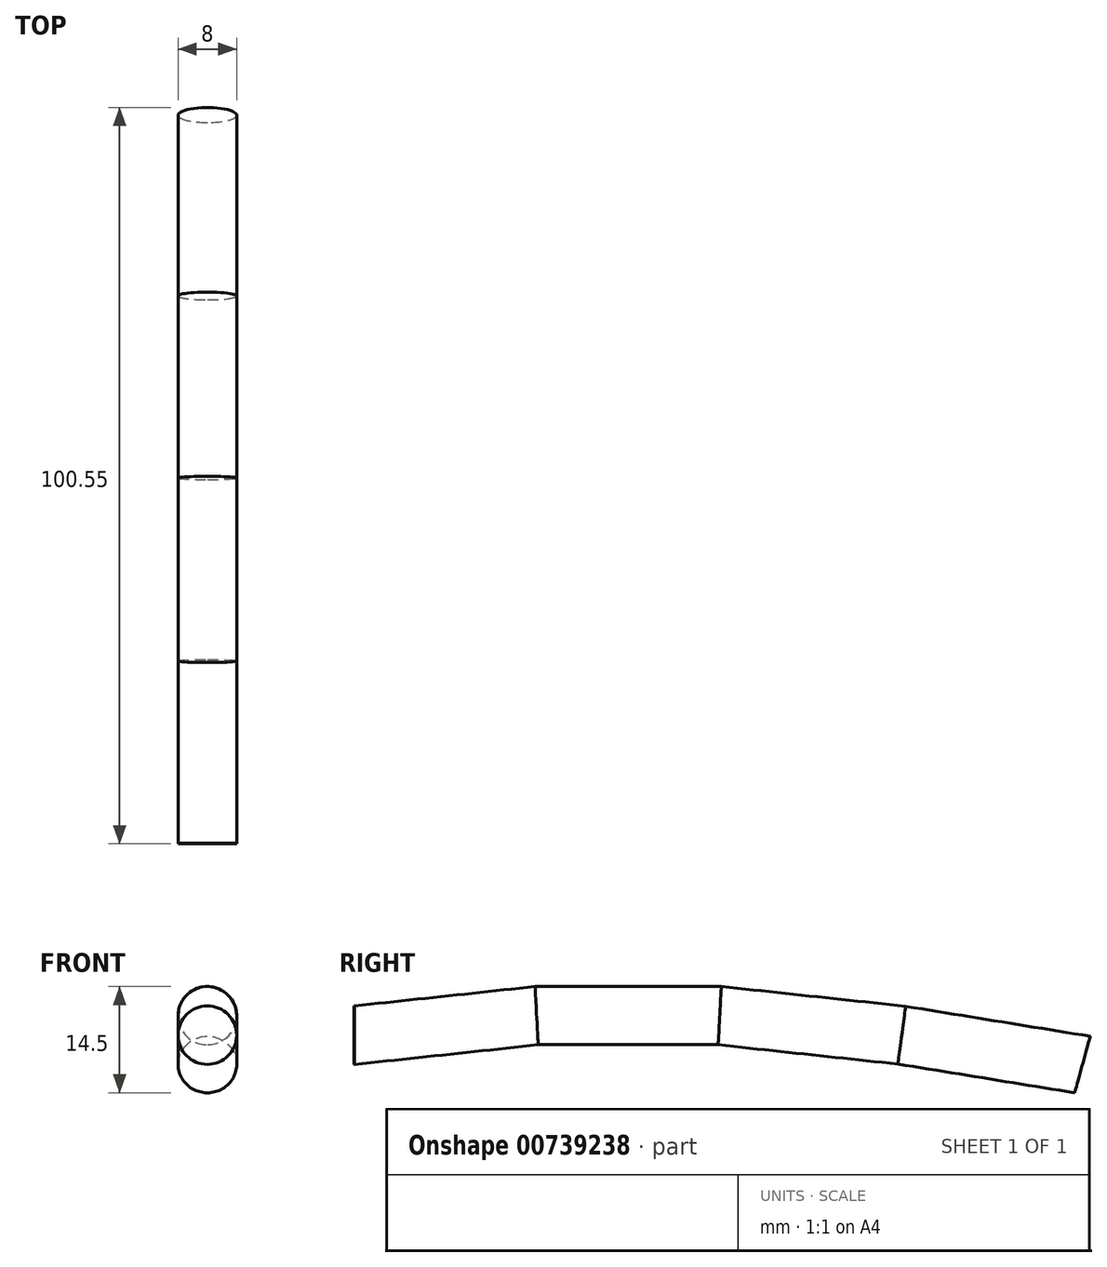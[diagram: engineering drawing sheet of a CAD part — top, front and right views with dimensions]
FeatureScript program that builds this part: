
annotation { "Feature Type Name" : "Feature", "Feature Type Description" : "" }
export const myFeature = defineFeature(function(context is Context, id is Id, definition is map)
    precondition{}
    {
        {
            var Q0;
            Q0=qCreatedBy(makeId("Front.planeOp"),FACE);
            var sketch = newSketch(context, id + "F0", { "sketchPlane" : qUnion([Q0])});
            skCircle(sketch, "E0", {"center": v(-0.51, 0) * mm, "radius": 4 * mm});
            skSolve(sketch);
        }
        {
            var Q0;
            Q0=qCreatedBy(makeId("Right.planeOp"),FACE);
            var sketch = newSketch(context, id + "F1", { "sketchPlane" : qUnion([Q0])});
            skLineSegment(sketch, "E1", {"start": v(0, 0) * mm, "end": v(24.86, 2.66) * mm});
            skLineSegment(sketch, "E2", {"start": v(24.86, 2.66) * mm, "end": v(49.86, 2.66) * mm});
            skLineSegment(sketch, "E3", {"start": v(49.86, 2.66) * mm, "end": v(74.72, 0) * mm});
            skLineSegment(sketch, "E4", {"start": v(74.72, 0) * mm, "end": v(99.4, -4) * mm});
            skSolve(sketch);
        }
        {
            var Q0;
            Q0 = qSketchRegion(id + "F0", true);
            extrude(context, id + "F2", {"entities" : qUnion([Q0]), "depth" : 0.1 * mm, "offsetDistance" : 25.4 * mm});
        }
        {
            var Q0;
            Q0=makeQuery(id+"F2.opExtrude","CAP_FACE",FACE,{"disambiguationData":[OSD([sQuery(id+"F0.wireOp",EDGE,"E0")])],"isStart":true});
            var Q1;
            Q1=sQuery(id+"F1.wireOp",EDGE,"E1");
            var Q2;
            Q2=sQuery(id+"F1.wireOp",EDGE,"E2");
            var Q3;
            Q3=sQuery(id+"F1.wireOp",EDGE,"E3");
            var Q4;
            Q4=sQuery(id+"F1.wireOp",EDGE,"E4");
            sweep(context, id + "F3", {"operationType" : NewBodyOperationType.ADD, "profiles" : qUnion([Q0]), "path" : qUnion([Q1, Q2, Q3, Q4])});
        }
    });
